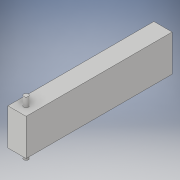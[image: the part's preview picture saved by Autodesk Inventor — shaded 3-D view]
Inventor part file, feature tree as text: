
AUTODESK INVENTOR PART (.ipt)
format: ipt  version: 2017 (Build 210142000, 142)  size: 108,032 bytes
history: native  units: in
note: dims shown in document units (in); Inventor stores cm internally (conversion verified against a paired STEP export)
features: extrude x3, sketch x3, projected_geometry x2
ambient origin geometry x8: Origin, YZ Plane, XZ Plane, XY Plane, X Axis, Y Axis, Z Axis, Center Point
bodies: Solid1 (feature_tree)
feature tree (8):
  extrude  "Extrusion1"  Depth=8.0in
  extrude  "Extrusion2"  Depth=1.0in
  extrude  "Extrusion3"  Depth=0.5in
  sketch  "Sketch1"  dims[d0=2.0in d1=8.0in]
  sketch  "Sketch2"  dims[d2=1.0in d3=0.0in d4=0.25in]
  projected_geometry  "Projected Loop1"
  sketch  "Sketch3"  dims[d5=0.5in d6=0.5in d7=0.5in d8=0.0in d9=0.25in d10=0.5in d11=0.5in d12=0.5in d13=0.0in]
  projected_geometry  "Projected Loop2"
